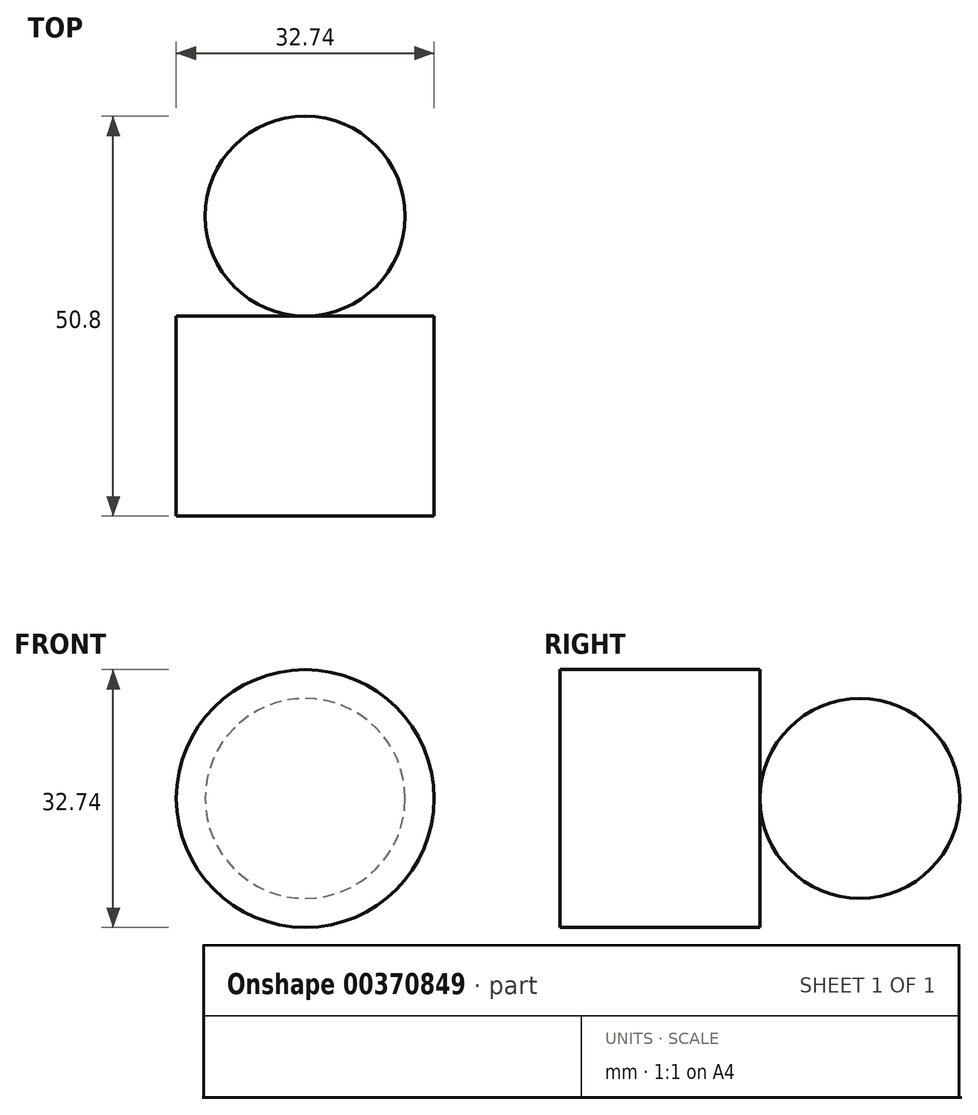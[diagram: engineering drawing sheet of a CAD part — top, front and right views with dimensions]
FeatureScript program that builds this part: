
annotation { "Feature Type Name" : "Feature", "Feature Type Description" : "" }
export const myFeature = defineFeature(function(context is Context, id is Id, definition is map)
    precondition{}
    {
        {
            var Q0;
            Q0=qCreatedBy(makeId("Front.planeOp"),FACE);
            var sketch = newSketch(context, id + "F0", { "sketchPlane" : qUnion([Q0])});
            skCircle(sketch, "E0", {"center": v(0, 0) * mm, "radius": 12.7 * mm});
            skSolve(sketch);
        }
        {
            var Q0;
            Q0=makeQuery(id+"F0.imprint","IMPRINT",FACE,{"disambiguationData":[TD([[makeQuery(id+"F0.imprint","IMPRINT",EDGE,{"derivedFrom":sQuery(id+"F0.wireOp",EDGE,"E0")}),1.0]])]});
            extrude(context, id + "F1", {"entities" : qUnion([Q0]), "endBound" : BoundingType.SYMMETRIC, "depth" : 25.4 * mm});
        }
        {
            var Q0;
            Q0=makeQuery(id+"F1.opExtrude","CAP_EDGE",EDGE,{"disambiguationData":[OSD([sQuery(id+"F0.wireOp",EDGE,"E0")])],"isStart":false});
            var Q1;
            Q1=makeQuery(id+"F1.opExtrude","CAP_EDGE",EDGE,{"disambiguationData":[OSD([sQuery(id+"F0.wireOp",EDGE,"E0")])],"isStart":true});
            fillet(context, id + "F2", {"entities" : qUnion([Q0, Q1]), "radius" : 12.7 * mm, "tangentPropagation" : true, "allowEdgeOverflow" : false});
        }
        {
            var Q0;
            Q0=qCreatedBy(makeId("Front.planeOp"),FACE);
            cPlane(context, id + "F3", {"entities" : qUnion([Q0]), "cplaneType" : CPlaneType.OFFSET, "offset" : 12.7 * mm, "width" : 152.4 * mm, "height" : 152.4 * mm});
        }
        {
            var Q0;
            Q0=qCreatedBy(id+"F3.planeOp",FACE);
            var sketch = newSketch(context, id + "F4", { "sketchPlane" : qUnion([Q0])});
            skCircle(sketch, "E1", {"center": v(0, 0) * mm, "radius": 16.37 * mm});
            skSolve(sketch);
        }
        {
            var Q0;
            Q0=makeQuery(id+"F4.imprint","IMPRINT",FACE,{"disambiguationData":[TD([[makeQuery(id+"F4.imprint","IMPRINT",EDGE,{"derivedFrom":sQuery(id+"F4.wireOp",EDGE,"E1")}),1.0]])]});
            extrude(context, id + "F5", {"entities" : qUnion([Q0]), "depth" : 25.4 * mm});
        }
    });
